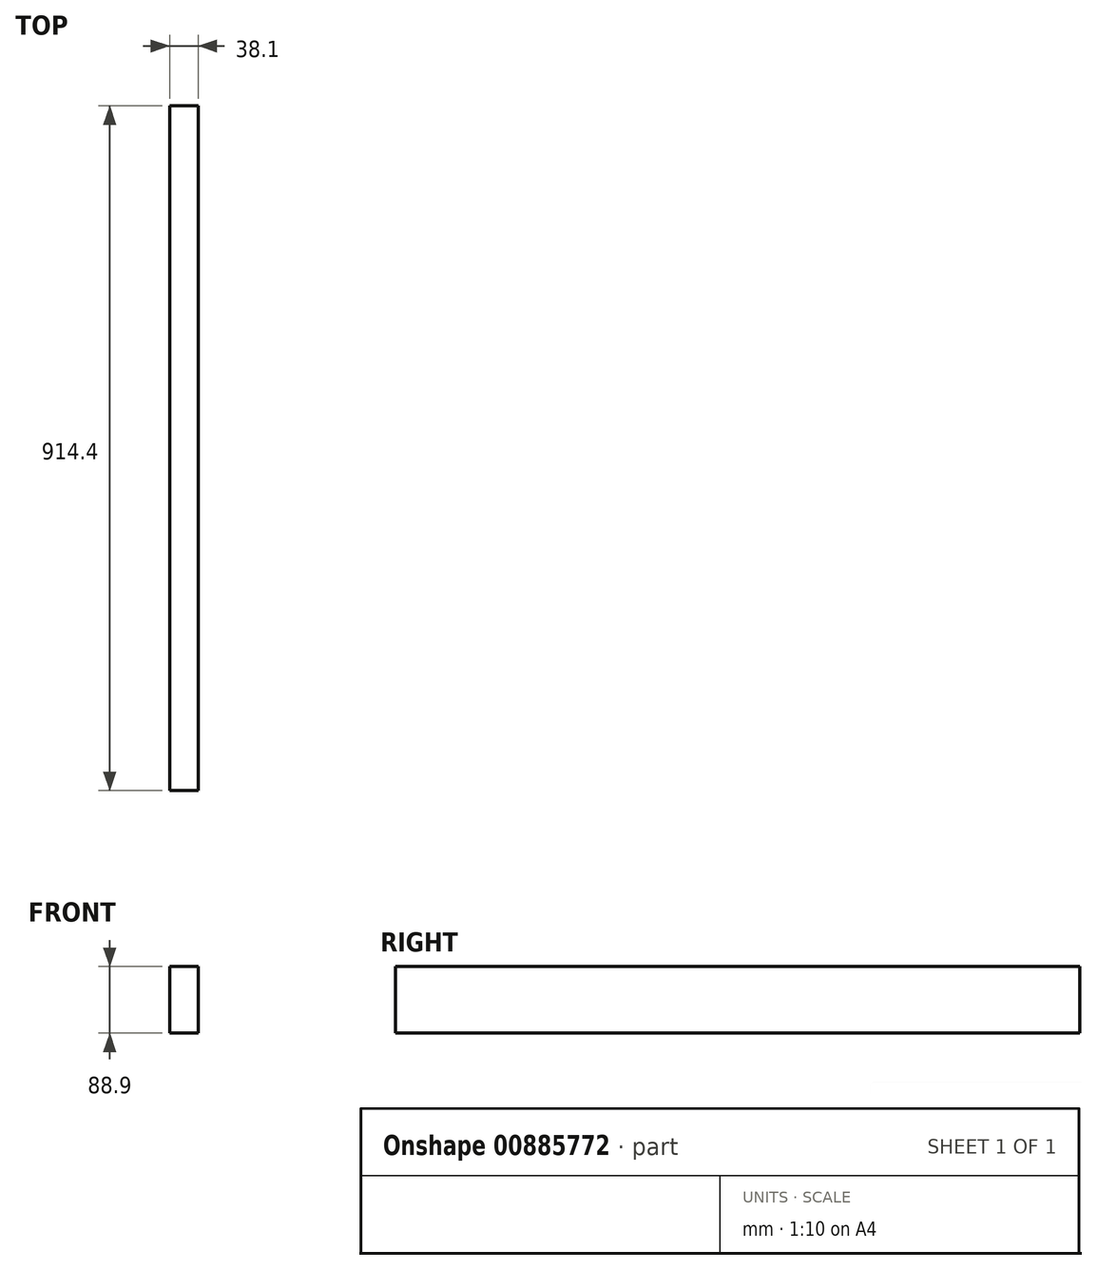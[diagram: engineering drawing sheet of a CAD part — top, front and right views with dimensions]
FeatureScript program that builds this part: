
annotation { "Feature Type Name" : "Feature", "Feature Type Description" : "" }
export const myFeature = defineFeature(function(context is Context, id is Id, definition is map)
    precondition{}
    {
        {
            var Q0;
            Q0=qCreatedBy(makeId("Front.planeOp"),FACE);
            var sketch = newSketch(context, id + "F0", { "sketchPlane" : qUnion([Q0])});
            skLineSegment(sketch, "E0.bottom", {"start": v(19.05, -44.45) * mm, "end": v(-19.05, -44.45) * mm});
            skLineSegment(sketch, "E0.top", {"start": v(19.05, 44.45) * mm, "end": v(-19.05, 44.45) * mm});
            skLineSegment(sketch, "E0.left", {"start": v(19.05, -44.45) * mm, "end": v(19.05, 44.45) * mm});
            skLineSegment(sketch, "E0.right", {"start": v(-19.05, -44.45) * mm, "end": v(-19.05, 44.45) * mm});
            skPoint(sketch, "E0.middle", {"position": v(0, 0) * mm});
            skSolve(sketch);
        }
        {
            var Q0;
            Q0=makeQuery(id+"F0.imprint","IMPRINT",FACE,{"disambiguationData":[TD([[makeQuery(id+"F0.imprint","IMPRINT",EDGE,{"derivedFrom":sQuery(id+"F0.wireOp",EDGE,"E0.bottom")}),-1.0]])]});
            extrude(context, id + "F1", {"entities" : qUnion([Q0]), "endBound" : BoundingType.SYMMETRIC, "depth" : 914.4 * mm, "offsetDistance" : 25.4 * mm});
        }
    });
